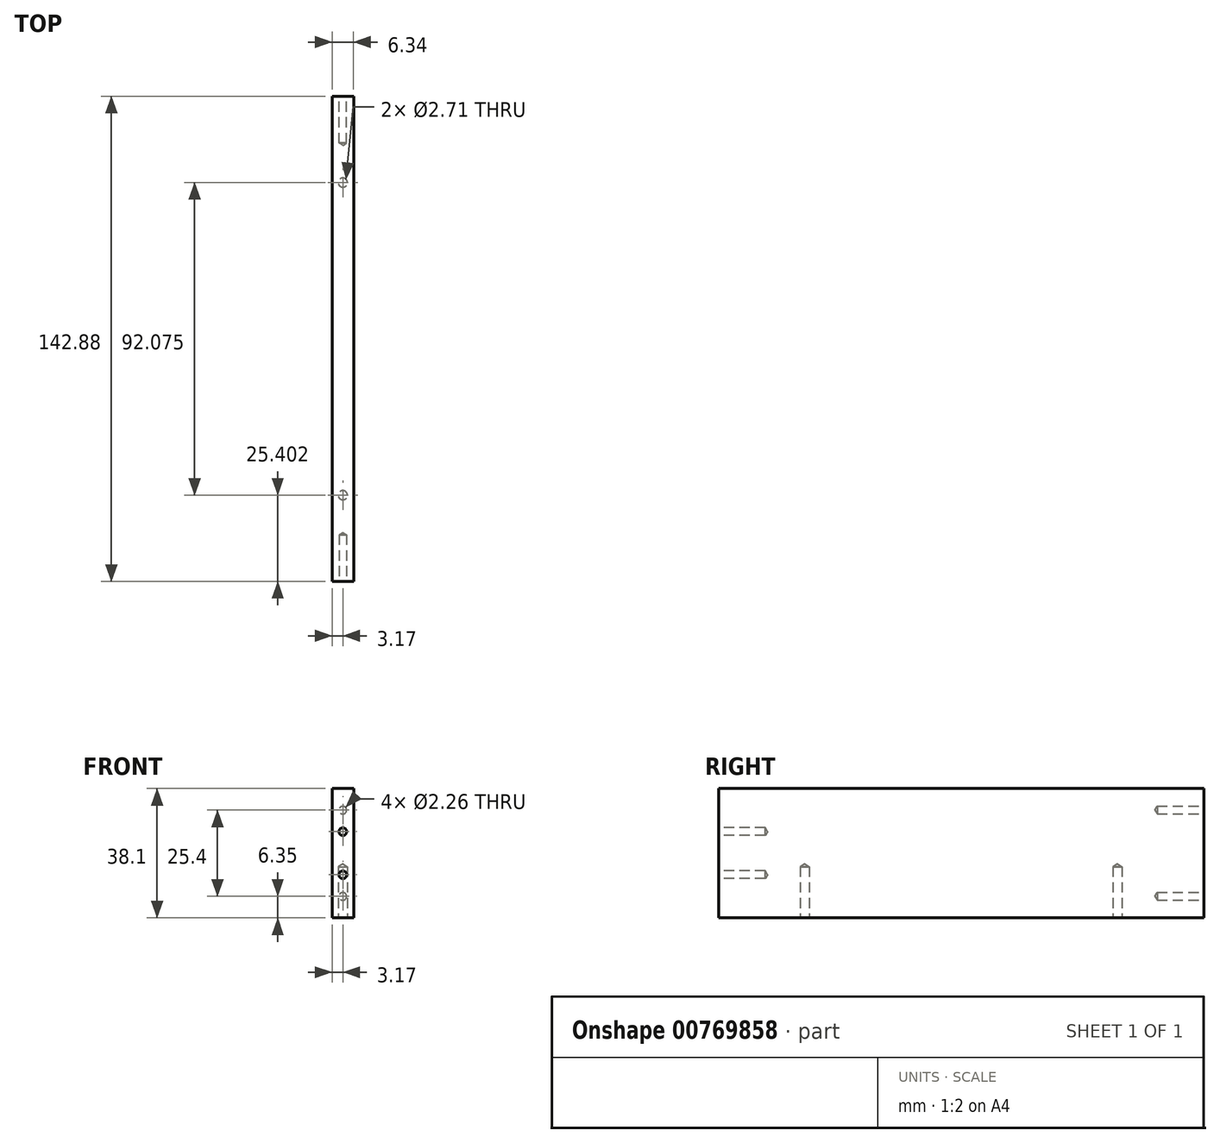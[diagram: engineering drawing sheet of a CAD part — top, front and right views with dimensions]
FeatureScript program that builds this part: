
annotation { "Feature Type Name" : "Feature", "Feature Type Description" : "" }
export const myFeature = defineFeature(function(context is Context, id is Id, definition is map)
    precondition{}
    {
        {
            var Q0;
            Q0=qCreatedBy(makeId("Top.planeOp"),FACE);
            var sketch = newSketch(context, id + "F0", { "sketchPlane" : qUnion([Q0])});
            skLineSegment(sketch, "E0.bottom", {"start": v(-3.17, 71.44) * mm, "end": v(3.18, 71.44) * mm});
            skLineSegment(sketch, "E0.top", {"start": v(-3.18, -71.44) * mm, "end": v(3.17, -71.44) * mm});
            skLineSegment(sketch, "E0.left", {"start": v(-3.17, 71.44) * mm, "end": v(-3.18, -71.44) * mm});
            skLineSegment(sketch, "E0.right", {"start": v(3.18, 71.44) * mm, "end": v(3.17, -71.44) * mm});
            skLineSegment(sketch, "E1", {"start": v(3.18, 71.44) * mm, "end": v(-3.18, -71.44) * mm, "construction": true});
            skSolve(sketch);
        }
        {
            var Q0;
            Q0=qSketchRegion(id+"F0",true);
            extrude(context, id + "F1", {"entities" : qUnion([Q0]), "depth" : 38.1 * mm, "offsetDistance" : 25.4 * mm});
        }
        {
            var Q0;
            Q0=makeQuery(id+"F1.opExtrude","CAP_FACE",FACE,{"disambiguationData":[OSD([sQuery(id+"F0.wireOp",EDGE,"E0.bottom"),sQuery(id+"F0.wireOp",EDGE,"E0.top"),sQuery(id+"F0.wireOp",EDGE,"E0.left"),sQuery(id+"F0.wireOp",EDGE,"E0.right")])],"isStart":true});
            var sketch = newSketch(context, id + "F2", { "sketchPlane" : qUnion([Q0])});
            skLineSegment(sketch, "E2", {"start": v(0, 71.44) * mm, "end": v(0, -71.44) * mm, "construction": true});
            skPoint(sketch, "E3", {"position": v(0, 46.04) * mm});
            skPoint(sketch, "E4", {"position": v(0, -46.04) * mm});
            skSolve(sketch);
        }
        {
            var Q0;
            Q0=sQuery(id+"F2.wireOp",VERTEX,"E3");
            var Q1;
            Q1=sQuery(id+"F2.wireOp",VERTEX,"E4");
            var Q2;
            Q2=makeQuery(id+"F1.opExtrude","SWEPT_BODY",BODY,{"disambiguationData":[OSD([sQuery(id+"F0.wireOp",EDGE,"E0.bottom"),sQuery(id+"F0.wireOp",EDGE,"E0.top"),sQuery(id+"F0.wireOp",EDGE,"E0.left"),sQuery(id+"F0.wireOp",EDGE,"E0.right")])]});
            hole(context, id + "F3", {"style" : HoleStyle.SIMPLE, "endStyle" : HoleEndStyle.BLIND, "standardTappedOrClearance" : lookupTablePath({ "standard" : "ANSI", "engagement" : "75%", "pitch" : "32 tpi", "size" : "#6", "type" : "Tapped" }), "standardBlindInLast" : lookupTablePath({ "standard" : "ANSI", "engagement" : "75%", "pitch" : "32 tpi", "size" : "#6", "type" : "Tapped" }), "holeDiameter" : 2.7 * mm, "majorDiameter" : 3.5 * mm, "showTappedDepth" : true, "holeDepth" : 15.1 * mm, "tappedDepth" : 12.7 * mm, "tapClearance" : 3, "locations" : qUnion([Q0, Q1]), "scope" : qUnion([Q2])});
        }
        {
            var Q0;
            Q0=makeQuery(id+"F1.opExtrude","SWEPT_FACE",FACE,{"disambiguationData":[OSD([sQuery(id+"F0.wireOp",EDGE,"E0.bottom")])]});
            var sketch = newSketch(context, id + "F4", { "sketchPlane" : qUnion([Q0])});
            skLineSegment(sketch, "E5", {"start": v(0, 38.1) * mm, "end": v(0, 0) * mm, "construction": true});
            skPoint(sketch, "E6", {"position": v(0, 25.4) * mm});
            skPoint(sketch, "E7", {"position": v(0, 12.7) * mm});
            skPoint(sketch, "E8", {"position": v(0, 19.05) * mm});
            skPoint(sketch, "E9", {"position": v(0, 31.75) * mm});
            skPoint(sketch, "E10", {"position": v(0, 6.35) * mm});
            skSolve(sketch);
        }
        {
            var Q0;
            Q0=makeQuery(id+"F1.opExtrude","SWEPT_FACE",FACE,{"disambiguationData":[OSD([sQuery(id+"F0.wireOp",EDGE,"E0.top")])]});
            var sketch = newSketch(context, id + "F5", { "sketchPlane" : qUnion([Q0])});
            skLineSegment(sketch, "E11", {"start": v(0, 38.1) * mm, "end": v(0, 0) * mm, "construction": true});
            skPoint(sketch, "E12", {"position": v(0, 31.75) * mm});
            skPoint(sketch, "E13", {"position": v(0, 6.35) * mm});
            skPoint(sketch, "E14", {"position": v(0, 19.05) * mm});
            skPoint(sketch, "E15", {"position": v(0, 25.4) * mm});
            skPoint(sketch, "E16", {"position": v(0, 12.7) * mm});
            skSolve(sketch);
        }
        {
            var Q0;
            Q0=sQuery(id+"F5.wireOp",VERTEX,"E15");
            var Q1;
            Q1=sQuery(id+"F5.wireOp",VERTEX,"E16");
            var Q2;
            Q2=sQuery(id+"F4.wireOp",VERTEX,"E9");
            var Q3;
            Q3=sQuery(id+"F4.wireOp",VERTEX,"E10");
            var Q4;
            Q4=makeQuery(id+"F1.opExtrude","SWEPT_BODY",BODY,{"disambiguationData":[OSD([sQuery(id+"F0.wireOp",EDGE,"E0.bottom"),sQuery(id+"F0.wireOp",EDGE,"E0.top"),sQuery(id+"F0.wireOp",EDGE,"E0.left"),sQuery(id+"F0.wireOp",EDGE,"E0.right")])]});
            hole(context, id + "F6", {"style" : HoleStyle.SIMPLE, "endStyle" : HoleEndStyle.BLIND, "standardTappedOrClearance" : lookupTablePath({ "standard" : "ANSI", "engagement" : "75%", "pitch" : "40 tpi", "size" : "#4", "type" : "Tapped" }), "standardBlindInLast" : lookupTablePath({ "standard" : "ANSI", "engagement" : "75%", "pitch" : "40 tpi", "size" : "#4", "type" : "Tapped" }), "holeDiameter" : 2.26 * mm, "majorDiameter" : 2.84 * mm, "showTappedDepth" : true, "holeDepth" : 13.74 * mm, "tappedDepth" : 11.84 * mm, "tapClearance" : 3, "startFromSketch" : true, "locations" : qUnion([Q0, Q1, Q2, Q3]), "scope" : qUnion([Q4])});
        }
    });
